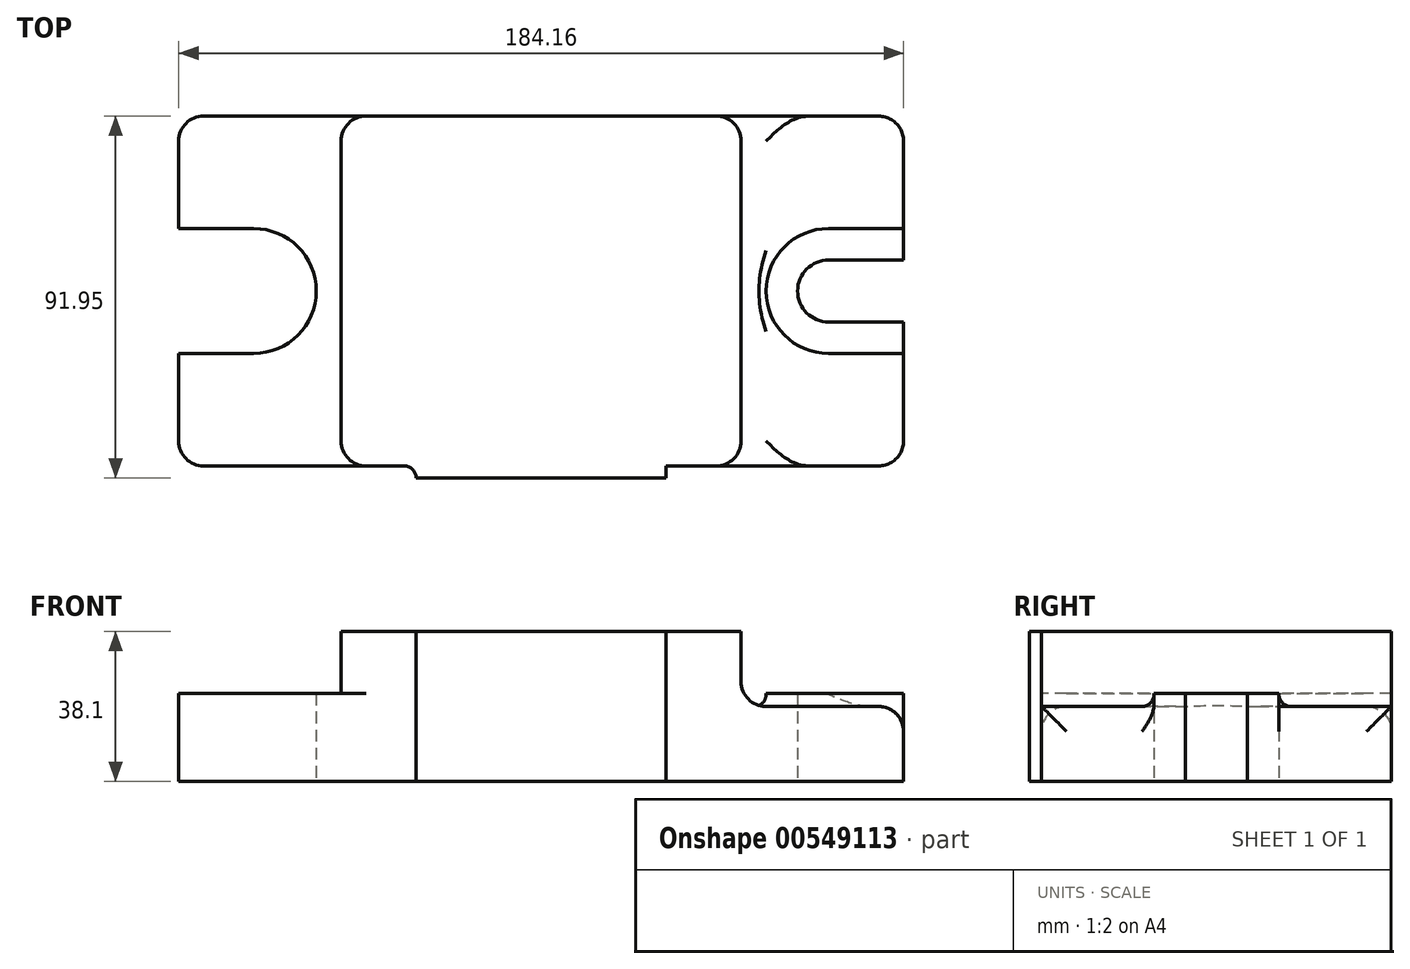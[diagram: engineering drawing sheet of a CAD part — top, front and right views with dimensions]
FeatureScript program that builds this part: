
annotation { "Feature Type Name" : "Feature", "Feature Type Description" : "" }
export const myFeature = defineFeature(function(context is Context, id is Id, definition is map)
    precondition{}
    {
        {
            var Q0;
            Q0=qCreatedBy(makeId("Top.planeOp"),FACE);
            var sketch = newSketch(context, id + "F0", { "sketchPlane" : qUnion([Q0])});
            skLineSegment(sketch, "E0.bottom", {"start": v(92.08, -44.45) * mm, "end": v(-92.07, -44.45) * mm});
            skLineSegment(sketch, "E0.top", {"start": v(92.07, 44.45) * mm, "end": v(-92.07, 44.45) * mm});
            skLineSegment(sketch, "E0.left", {"start": v(92.08, -44.45) * mm, "end": v(92.08, 44.45) * mm});
            skLineSegment(sketch, "E0.right", {"start": v(-92.07, -44.45) * mm, "end": v(-92.07, 44.45) * mm});
            skPoint(sketch, "E0.middle", {"position": v(0, 0) * mm});
            skLineSegment(sketch, "E1", {"start": v(-50.8, 44.45) * mm, "end": v(-50.8, -44.45) * mm});
            skLineSegment(sketch, "E2", {"start": v(0, 44.45) * mm, "end": v(0, -44.45) * mm, "construction": true});
            skLineSegment(sketch, "E3.MirrorCS", {"start": v(50.8, 44.45) * mm, "end": v(50.8, -44.45) * mm});
            skLineSegment(sketch, "E4", {"start": v(-92.07, 0) * mm, "end": v(-73.03, 0) * mm, "construction": true});
            skArc(sketch, "E5.0.startCap", {"start": v(-92.07, -15.87) * mm, "mid": v(-107.95, 0) * mm, "end": v(-92.07, 15.88) * mm});
            skArc(sketch, "E5.0.endCap", {"start": v(-73.03, 15.88) * mm, "mid": v(-57.15, 0) * mm, "end": v(-73.03, -15.87) * mm});
            skLineSegment(sketch, "E5.0.left", {"start": v(-92.07, 15.88) * mm, "end": v(-73.03, 15.88) * mm});
            skLineSegment(sketch, "E5.0.right", {"start": v(-92.07, -15.87) * mm, "end": v(-73.03, -15.87) * mm});
            skArc(sketch, "E6.0.startCap", {"start": v(-92.07, -7.87) * mm, "mid": v(-99.95, 0) * mm, "end": v(-92.07, 7.87) * mm});
            skArc(sketch, "E6.0.endCap", {"start": v(-73.03, 7.87) * mm, "mid": v(-65.15, 0) * mm, "end": v(-73.03, -7.87) * mm});
            skLineSegment(sketch, "E6.0.left", {"start": v(-92.07, 7.87) * mm, "end": v(-73.03, 7.87) * mm});
            skLineSegment(sketch, "E6.0.right", {"start": v(-92.07, -7.87) * mm, "end": v(-73.03, -7.87) * mm});
            skArc(sketch, "E7.MirrorCS", {"start": v(73.03, 15.88) * mm, "mid": v(57.15, 0) * mm, "end": v(73.03, -15.87) * mm});
            skLineSegment(sketch, "E8.MirrorCS", {"start": v(92.07, 15.88) * mm, "end": v(73.03, 15.88) * mm});
            skArc(sketch, "E9.MirrorCS", {"start": v(73.03, 7.87) * mm, "mid": v(65.15, 0) * mm, "end": v(73.03, -7.87) * mm});
            skLineSegment(sketch, "E10.MirrorCS", {"start": v(92.07, 7.87) * mm, "end": v(73.03, 7.87) * mm});
            skLineSegment(sketch, "E11.MirrorCS", {"start": v(92.07, 0) * mm, "end": v(73.03, 0) * mm, "construction": true});
            skLineSegment(sketch, "E12.MirrorCS", {"start": v(92.07, -7.87) * mm, "end": v(73.03, -7.87) * mm});
            skLineSegment(sketch, "E13.MirrorCS", {"start": v(92.07, -15.87) * mm, "end": v(73.03, -15.87) * mm});
            skSolve(sketch);
        }
        {
            var Q0;
            {var subQ4=sQuery(id+"F0.wireOp",EDGE,"E3.MirrorCS");Q0=makeQuery(id+"F0.imprint","IMPRINT",FACE,{"disambiguationData":[TD([[makeQuery(id+"F0.imprint","IMPRINT",EDGE,{"derivedFrom":subQ4}),1.0]])]});}
            var Q1;
            {var subQ0=sQuery(id+"F0.wireOp",EDGE,"E1");Q1=makeQuery(id+"F0.imprint","IMPRINT",FACE,{"disambiguationData":[TD([[makeQuery(id+"F0.imprint","IMPRINT",EDGE,{"derivedFrom":subQ0}),1.0]])]});}
            var Q2;
            {var subQ8=sQuery(id+"F0.wireOp",EDGE,"E1");Q2=makeQuery(id+"F0.imprint","IMPRINT",FACE,{"disambiguationData":[TD([[makeQuery(id+"F0.imprint","IMPRINT",EDGE,{"derivedFrom":subQ8}),-1.0]])]});}
            var Q3;
            Q3=makeQuery(id+"F0.imprint","IMPRINT",FACE,{"disambiguationData":[TD([[makeQuery(id+"F0.imprint","IMPRINT",EDGE,{"derivedFrom":sQuery(id+"F0.wireOp",EDGE,"E7.MirrorCS")}),1.0]])]});
            var Q4;
            Q4=makeQuery(id+"F0.imprint","IMPRINT",FACE,{"disambiguationData":[TD([[makeQuery(id+"F0.imprint","IMPRINT",EDGE,{"derivedFrom":sQuery(id+"F0.wireOp",EDGE,"E5.0.endCap")}),-1.0]])]});
            extrude(context, id + "F1", {"entities" : qUnion([Q0, Q1, Q2, Q3, Q4]), "depth" : 19.05 * mm, "offsetDistance" : 25.4 * mm});
        }
        {
            var Q0;
            {var subQ0=sQuery(id+"F0.wireOp",EDGE,"E1");Q0=makeQuery(id+"F0.imprint","IMPRINT",FACE,{"disambiguationData":[TD([[makeQuery(id+"F0.imprint","IMPRINT",EDGE,{"derivedFrom":subQ0}),1.0]])]});}
            extrude(context, id + "F2", {"entities" : qUnion([Q0]), "operationType" : NewBodyOperationType.ADD, "depth" : 38.1 * mm, "offsetDistance" : 25.4 * mm});
        }
        {
            var Q0;
            Q0=makeQuery(id+"F0.imprint","IMPRINT",FACE,{"disambiguationData":[TD([[makeQuery(id+"F0.imprint","IMPRINT",EDGE,{"derivedFrom":sQuery(id+"F0.wireOp",EDGE,"E5.0.endCap")}),-1.0]])]});
            var Q1;
            Q1=makeQuery(id+"F0.imprint","IMPRINT",FACE,{"disambiguationData":[TD([[makeQuery(id+"F0.imprint","IMPRINT",EDGE,{"derivedFrom":sQuery(id+"F0.wireOp",EDGE,"E7.MirrorCS")}),1.0]])]});
            extrude(context, id + "F3", {"entities" : qUnion([Q0, Q1]), "operationType" : NewBodyOperationType.ADD, "depth" : 22.35 * mm, "offsetDistance" : 25.4 * mm});
        }
        {
            var Q0;
            {var subQ0=sQuery(id+"F0.wireOp",EDGE,"E0.bottom");Q0=makeQuery(id+"F2.boolean.opBoolean","MERGE",FACE,{"derivedFrom":[makeQuery(id+"F1.opExtrude","SWEPT_FACE",FACE,{"disambiguationData":[OSD([subQ0])]}),makeQuery(id+"F2.opExtrude","SWEPT_FACE",FACE,{"disambiguationData":[OSD([subQ0])]})]});}
            var sketch = newSketch(context, id + "F4", { "sketchPlane" : qUnion([Q0])});
            skLineSegment(sketch, "E14.bottom", {"start": v(31.75, 0) * mm, "end": v(-31.75, 0) * mm});
            skLineSegment(sketch, "E14.top", {"start": v(31.75, 38.1) * mm, "end": v(-31.75, 38.1) * mm});
            skLineSegment(sketch, "E14.left", {"start": v(31.75, 0) * mm, "end": v(31.75, 38.1) * mm});
            skLineSegment(sketch, "E14.right", {"start": v(-31.75, 0) * mm, "end": v(-31.75, 38.1) * mm});
            skPoint(sketch, "E14.middle", {"position": v(0, 19.05) * mm});
            skSolve(sketch);
        }
        {
            var Q0;
            Q0 = qSketchRegion(id + "F4", true);
            extrude(context, id + "F5", {"entities" : qUnion([Q0]), "operationType" : NewBodyOperationType.ADD, "depth" : 3.05 * mm, "offsetDistance" : 25.4 * mm});
        }
        {
            var Q0;
            Q0=makeQuery(id+"F1.opExtrude","SWEPT_EDGE",EDGE,{"disambiguationData":[OSD([sQuery(id+"F0.wireOp",EDGE,"E0.bottom"),sQuery(id+"F0.wireOp",EDGE,"E0.left")])]});
            var Q1;
            Q1=makeQuery(id+"F2.opExtrude","SWEPT_EDGE",EDGE,{"disambiguationData":[OSD([sQuery(id+"F0.wireOp",EDGE,"E0.bottom"),sQuery(id+"F0.wireOp",EDGE,"E3.MirrorCS")])]});
            var Q2;
            Q2=makeQuery(id+"F1.opExtrude","SWEPT_EDGE",EDGE,{"disambiguationData":[OSD([sQuery(id+"F0.wireOp",EDGE,"E0.top"),sQuery(id+"F0.wireOp",EDGE,"E0.left")])]});
            var Q3;
            Q3=makeQuery(id+"F2.opExtrude","SWEPT_EDGE",EDGE,{"disambiguationData":[OSD([sQuery(id+"F0.wireOp",EDGE,"E0.top"),sQuery(id+"F0.wireOp",EDGE,"E3.MirrorCS")])]});
            var Q4;
            Q4=makeQuery(id+"F2.boolean.opBoolean","INTERSECT",EDGE,{"derivedFrom":[makeQuery(id+"F1.opExtrude","CAP_FACE",FACE,{"disambiguationData":[OSD([sQuery(id+"F0.wireOp",EDGE,"E0.bottom"),sQuery(id+"F0.wireOp",EDGE,"E0.top"),sQuery(id+"F0.wireOp",EDGE,"E0.left"),sQuery(id+"F0.wireOp",EDGE,"E0.right"),sQuery(id+"F0.wireOp",EDGE,"E6.0.endCap"),sQuery(id+"F0.wireOp",EDGE,"E6.0.left"),sQuery(id+"F0.wireOp",EDGE,"E6.0.right"),sQuery(id+"F0.wireOp",EDGE,"E9.MirrorCS"),sQuery(id+"F0.wireOp",EDGE,"E10.MirrorCS"),sQuery(id+"F0.wireOp",EDGE,"E12.MirrorCS")])],"isStart":false}),makeQuery(id+"F2.opExtrude","SWEPT_FACE",FACE,{"disambiguationData":[OSD([sQuery(id+"F0.wireOp",EDGE,"E3.MirrorCS")])]})]});
            var Q5;
            Q5=makeQuery(id+"F2.boolean.opBoolean","INTERSECT",EDGE,{"derivedFrom":[makeQuery(id+"F1.opExtrude","CAP_FACE",FACE,{"disambiguationData":[OSD([sQuery(id+"F0.wireOp",EDGE,"E0.bottom"),sQuery(id+"F0.wireOp",EDGE,"E0.top"),sQuery(id+"F0.wireOp",EDGE,"E0.left"),sQuery(id+"F0.wireOp",EDGE,"E0.right"),sQuery(id+"F0.wireOp",EDGE,"E6.0.endCap"),sQuery(id+"F0.wireOp",EDGE,"E6.0.left"),sQuery(id+"F0.wireOp",EDGE,"E6.0.right"),sQuery(id+"F0.wireOp",EDGE,"E9.MirrorCS"),sQuery(id+"F0.wireOp",EDGE,"E10.MirrorCS"),sQuery(id+"F0.wireOp",EDGE,"E12.MirrorCS")])],"isStart":false}),makeQuery(id+"F2.opExtrude","SWEPT_FACE",FACE,{"disambiguationData":[OSD([sQuery(id+"F0.wireOp",EDGE,"E1")])]})]});
            var Q6;
            Q6=makeQuery(id+"F2.opExtrude","SWEPT_EDGE",EDGE,{"disambiguationData":[OSD([sQuery(id+"F0.wireOp",EDGE,"E0.bottom"),sQuery(id+"F0.wireOp",EDGE,"E1")])]});
            var Q7;
            Q7=makeQuery(id+"F2.opExtrude","SWEPT_EDGE",EDGE,{"disambiguationData":[OSD([sQuery(id+"F0.wireOp",EDGE,"E0.top"),sQuery(id+"F0.wireOp",EDGE,"E1")])]});
            var Q8;
            Q8=makeQuery(id+"F1.opExtrude","SWEPT_EDGE",EDGE,{"disambiguationData":[OSD([sQuery(id+"F0.wireOp",EDGE,"E0.bottom"),sQuery(id+"F0.wireOp",EDGE,"E0.right")])]});
            var Q9;
            Q9=makeQuery(id+"F1.opExtrude","SWEPT_EDGE",EDGE,{"disambiguationData":[OSD([sQuery(id+"F0.wireOp",EDGE,"E0.top"),sQuery(id+"F0.wireOp",EDGE,"E0.right")])]});
            var Q10;
            {var subQ0=sQuery(id+"F0.wireOp",EDGE,"E0.right");var subQ1=makeQuery(id+"F0.imprint","INTERSECT",VERTEX,{"derivedFrom":[subQ0,sQuery(id+"F0.wireOp",EDGE,"E5.0.startCap"),sQuery(id+"F0.wireOp",EDGE,"E5.0.left")]});Q10=makeQuery(id+"F1.opExtrude","CAP_EDGE",EDGE,{"disambiguationData":[OSD([subQ0]),TDD([makeQuery(id+"F0.imprint","IMPRINT",EDGE,{"disambiguationData":[TD([[subQ1,1.0]])],"derivedFrom":subQ0}),makeQuery(id+"F0.imprint","IMPRINT",EDGE,{"disambiguationData":[TD([[makeQuery(id+"F0.imprint","INTERSECT",VERTEX,{"derivedFrom":[sQuery(id+"F0.wireOp",EDGE,"E0.top"),subQ0]}),1.0]])],"derivedFrom":subQ0})])],"isStart":false});}
            var Q11;
            {var subQ0=sQuery(id+"F0.wireOp",EDGE,"E0.right");var subQ1=makeQuery(id+"F0.imprint","INTERSECT",VERTEX,{"derivedFrom":[subQ0,sQuery(id+"F0.wireOp",EDGE,"E5.0.startCap"),sQuery(id+"F0.wireOp",EDGE,"E5.0.right")]});Q11=makeQuery(id+"F1.opExtrude","CAP_EDGE",EDGE,{"disambiguationData":[OSD([subQ0]),TDD([makeQuery(id+"F0.imprint","IMPRINT",EDGE,{"disambiguationData":[TD([[makeQuery(id+"F0.imprint","INTERSECT",VERTEX,{"derivedFrom":[sQuery(id+"F0.wireOp",EDGE,"E0.bottom"),subQ0]}),-1.0]])],"derivedFrom":subQ0}),makeQuery(id+"F0.imprint","IMPRINT",EDGE,{"disambiguationData":[TD([[subQ1,-1.0]])],"derivedFrom":subQ0})])],"isStart":false});}
            var Q12;
            {var subQ0=sQuery(id+"F0.wireOp",EDGE,"E0.left");Q12=makeQuery(id+"F1.opExtrude","CAP_EDGE",EDGE,{"disambiguationData":[OSD([subQ0]),TDD([makeQuery(id+"F0.imprint","IMPRINT",EDGE,{"disambiguationData":[TD([[makeQuery(id+"F0.imprint","INTERSECT",VERTEX,{"derivedFrom":[sQuery(id+"F0.wireOp",EDGE,"E0.bottom"),subQ0]}),-1.0]])],"derivedFrom":subQ0}),makeQuery(id+"F0.imprint","IMPRINT",EDGE,{"disambiguationData":[TD([[makeQuery(id+"F0.imprint","INTERSECT",VERTEX,{"derivedFrom":[subQ0,sQuery(id+"F0.wireOp",EDGE,"E12.MirrorCS")]}),1.0]])],"derivedFrom":subQ0})])],"isStart":false});}
            var Q13;
            {var subQ0=sQuery(id+"F0.wireOp",EDGE,"E0.left");var subQ1=makeQuery(id+"F0.imprint","INTERSECT",VERTEX,{"derivedFrom":[subQ0,sQuery(id+"F0.wireOp",EDGE,"E8.MirrorCS")]});Q13=makeQuery(id+"F1.opExtrude","CAP_EDGE",EDGE,{"disambiguationData":[OSD([subQ0]),TDD([makeQuery(id+"F0.imprint","IMPRINT",EDGE,{"disambiguationData":[TD([[subQ1,1.0]])],"derivedFrom":subQ0}),makeQuery(id+"F0.imprint","IMPRINT",EDGE,{"disambiguationData":[TD([[makeQuery(id+"F0.imprint","INTERSECT",VERTEX,{"derivedFrom":[sQuery(id+"F0.wireOp",EDGE,"E0.top"),subQ0]}),1.0]])],"derivedFrom":subQ0})])],"isStart":false});}
            fillet(context, id + "F6", {"entities" : qUnion([Q0, Q1, Q2, Q3, Q4, Q5, Q6, Q7, Q8, Q9, Q10, Q11, Q12, Q13]), "radius" : 6.35 * mm, "tangentPropagation" : true, "allowEdgeOverflow" : false});
        }
        {
            var Q0;
            {var subQ0=sQuery(id+"F0.wireOp",EDGE,"E13.MirrorCS");var subQ1=sQuery(id+"F0.wireOp",EDGE,"E12.MirrorCS");var subQ2=sQuery(id+"F0.wireOp",EDGE,"E0.left");var subQ4=sQuery(id+"F0.wireOp",EDGE,"E0.bottom");var subQ5=sQuery(id+"F0.wireOp",EDGE,"E0.top");var subQ7=sQuery(id+"F0.wireOp",EDGE,"E10.MirrorCS");var subQ8=sQuery(id+"F0.wireOp",EDGE,"E9.MirrorCS");Q0=makeQuery(id+"F3.boolean.opBoolean","INTERSECT",EDGE,{"derivedFrom":[makeQuery(id+"F2.boolean.opBoolean","SPLIT",FACE,{"disambiguationData":[TD([makeQuery(id+"F1.opExtrude","SWEPT_FACE",FACE,{"disambiguationData":[OSD([subQ8])]})])],"derivedFrom":makeQuery(id+"F1.opExtrude","CAP_FACE",FACE,{"disambiguationData":[OSD([subQ4,subQ5,subQ2,sQuery(id+"F0.wireOp",EDGE,"E0.right"),sQuery(id+"F0.wireOp",EDGE,"E6.0.endCap"),sQuery(id+"F0.wireOp",EDGE,"E6.0.left"),sQuery(id+"F0.wireOp",EDGE,"E6.0.right"),subQ8,subQ7,subQ1])],"isStart":false})}),makeQuery(id+"F3.opExtrude","SWEPT_FACE",FACE,{"disambiguationData":[OSD([subQ0])]})]});}
            var Q1;
            Q1=makeQuery(id+"F5.opExtrude","CAP_EDGE",EDGE,{"disambiguationData":[OSD([sQuery(id+"F4.wireOp",EDGE,"E14.left")])],"isStart":true});
            var Q2;
            Q2=makeQuery(id+"F5.opExtrude","CAP_EDGE",EDGE,{"disambiguationData":[OSD([sQuery(id+"F4.wireOp",EDGE,"E14.right")])],"isStart":true});
            var Q3;
            {var subQ0=sQuery(id+"F0.wireOp",EDGE,"E0.right");var subQ1=sQuery(id+"F0.wireOp",EDGE,"E0.top");var subQ4=sQuery(id+"F0.wireOp",EDGE,"E6.0.left");var subQ7=sQuery(id+"F0.wireOp",EDGE,"E6.0.right");var subQ8=sQuery(id+"F0.wireOp",EDGE,"E0.bottom");var subQ9=sQuery(id+"F0.wireOp",EDGE,"E6.0.endCap");Q3=makeQuery(id+"F3.boolean.opBoolean","INTERSECT",EDGE,{"derivedFrom":[makeQuery(id+"F2.boolean.opBoolean","SPLIT",FACE,{"disambiguationData":[TD([makeQuery(id+"F1.opExtrude","SWEPT_FACE",FACE,{"disambiguationData":[OSD([subQ9])]})])],"derivedFrom":makeQuery(id+"F1.opExtrude","CAP_FACE",FACE,{"disambiguationData":[OSD([subQ8,subQ1,sQuery(id+"F0.wireOp",EDGE,"E0.left"),subQ0,subQ9,subQ4,subQ7,sQuery(id+"F0.wireOp",EDGE,"E9.MirrorCS"),sQuery(id+"F0.wireOp",EDGE,"E10.MirrorCS"),sQuery(id+"F0.wireOp",EDGE,"E12.MirrorCS")])],"isStart":false})}),makeQuery(id+"F3.opExtrude","SWEPT_FACE",FACE,{"disambiguationData":[OSD([sQuery(id+"F0.wireOp",EDGE,"E5.0.endCap")])]})]});}
            fillet(context, id + "F7", {"entities" : qUnion([Q0, Q1, Q2, Q3]), "radius" : 3.05 * mm, "tangentPropagation" : true, "allowEdgeOverflow" : false});
        }
    });
